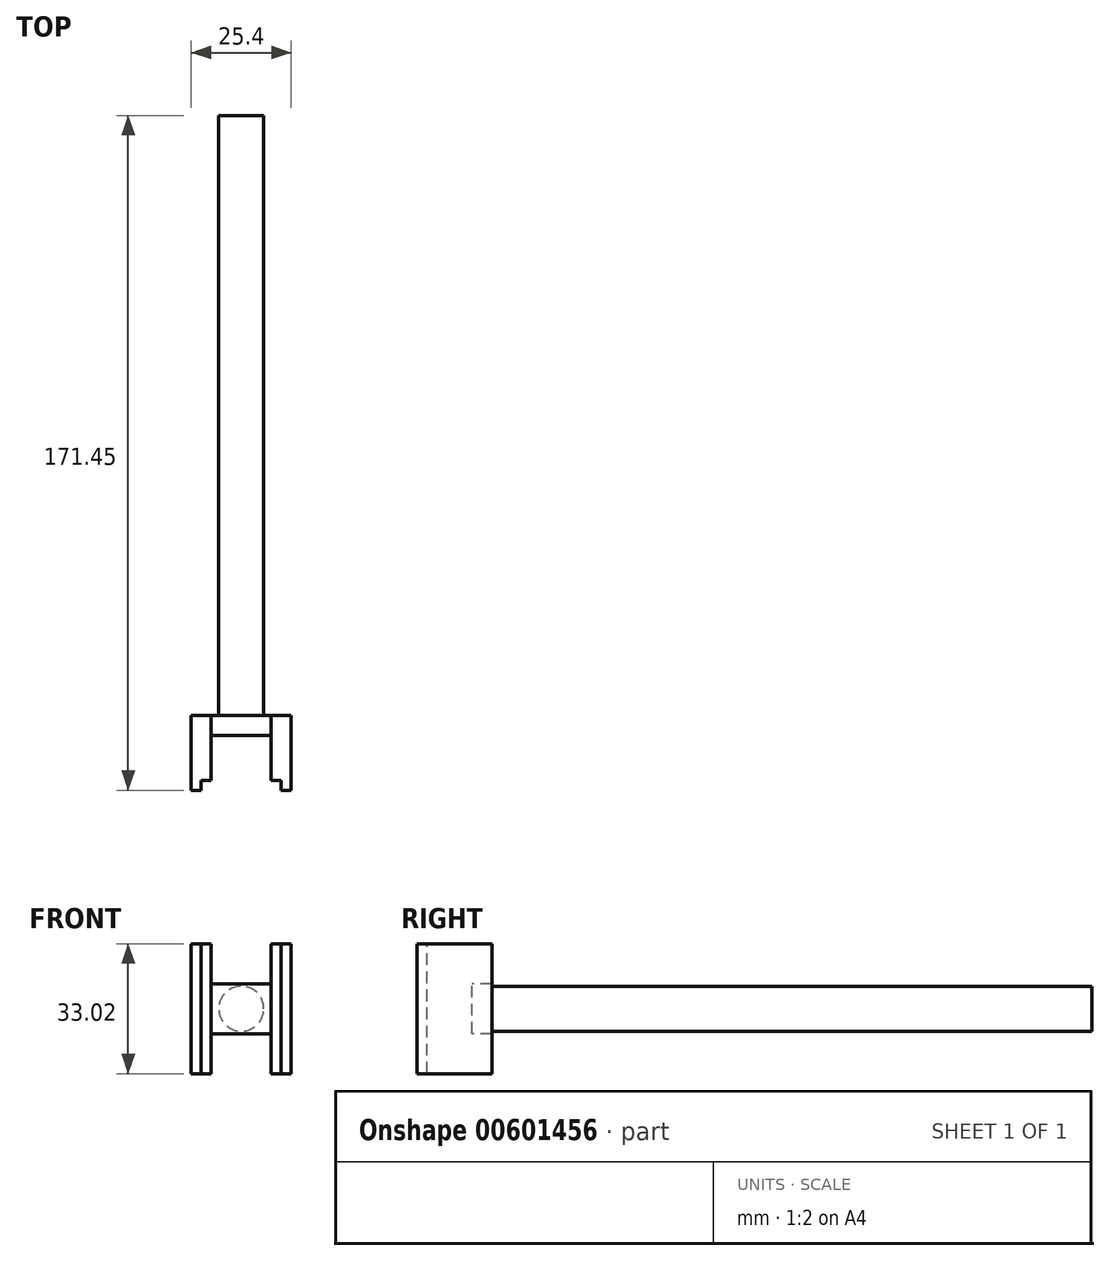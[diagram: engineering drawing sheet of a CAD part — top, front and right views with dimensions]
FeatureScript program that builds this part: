
annotation { "Feature Type Name" : "Feature", "Feature Type Description" : "" }
export const myFeature = defineFeature(function(context is Context, id is Id, definition is map)
    precondition{}
    {
        {
            var Q0;
            Q0=qCreatedBy(makeId("Front.planeOp"),FACE);
            var sketch = newSketch(context, id + "F0", { "sketchPlane" : qUnion([Q0])});
            skLineSegment(sketch, "E0.bottom", {"start": v(0, 0) * mm, "end": v(25.4, 0) * mm});
            skLineSegment(sketch, "E0.top", {"start": v(0, 33.02) * mm, "end": v(25.4, 33.02) * mm});
            skLineSegment(sketch, "E0.left", {"start": v(0, 0) * mm, "end": v(0, 33.02) * mm});
            skLineSegment(sketch, "E0.right", {"start": v(25.4, 0) * mm, "end": v(25.4, 33.02) * mm});
            skSolve(sketch);
        }
        {
            var Q0;
            Q0=makeQuery(id+"F0.imprint","IMPRINT",FACE,{"disambiguationData":[TD([[makeQuery(id+"F0.imprint","IMPRINT",EDGE,{"derivedFrom":sQuery(id+"F0.wireOp",EDGE,"E0.bottom")}),1.0]])]});
            var sketch = newSketch(context, id + "F1", { "sketchPlane" : qUnion([Q0])});
            skSolve(sketch);
        }
        {
            var Q0;
            Q0=makeQuery(id+"F0.imprint","IMPRINT",FACE,{"disambiguationData":[TD([[makeQuery(id+"F0.imprint","IMPRINT",EDGE,{"derivedFrom":sQuery(id+"F0.wireOp",EDGE,"E0.bottom")}),1.0]])]});
            extrude(context, id + "F2", {"entities" : qUnion([Q0]), "oppositeDirection" : true, "depth" : 19.05 * mm, "offsetDistance" : 25.4 * mm});
        }
        {
            var Q0;
            Q0=makeQuery(id+"F2.opExtrude","SWEPT_FACE",FACE,{"disambiguationData":[OSD([sQuery(id+"F0.wireOp",EDGE,"E0.top")])]});
            var sketch = newSketch(context, id + "F3", { "sketchPlane" : qUnion([Q0])});
            skLineSegment(sketch, "E1.bottom", {"start": v(5.08, 0) * mm, "end": v(20.32, 0) * mm});
            skLineSegment(sketch, "E1.top", {"start": v(5.08, 13.97) * mm, "end": v(20.32, 13.97) * mm});
            skLineSegment(sketch, "E1.left", {"start": v(5.08, 0) * mm, "end": v(5.08, 13.97) * mm});
            skLineSegment(sketch, "E1.right", {"start": v(20.32, 0) * mm, "end": v(20.32, 13.97) * mm});
            skSolve(sketch);
        }
        {
            var Q0;
            Q0=makeQuery(id+"F3.imprint","IMPRINT",FACE,{"disambiguationData":[TD([[makeQuery(id+"F3.imprint","IMPRINT",EDGE,{"derivedFrom":sQuery(id+"F3.wireOp",EDGE,"E1.bottom")}),1.0]])]});
            extrude(context, id + "F4", {"entities" : qUnion([Q0]), "operationType" : NewBodyOperationType.REMOVE, "endBound" : BoundingType.THROUGH_ALL, "oppositeDirection" : true, "depth" : 25.4 * mm, "offsetDistance" : 25.4 * mm});
        }
        {
            var Q0;
            Q0=makeQuery(id+"F2.opExtrude","SWEPT_FACE",FACE,{"disambiguationData":[OSD([sQuery(id+"F0.wireOp",EDGE,"E0.top")])]});
            var sketch = newSketch(context, id + "F5", { "sketchPlane" : qUnion([Q0])});
            skLineSegment(sketch, "E2.bottom", {"start": v(2.54, 0) * mm, "end": v(5.08, 0) * mm});
            skLineSegment(sketch, "E2.top", {"start": v(2.54, 2.54) * mm, "end": v(5.08, 2.54) * mm});
            skLineSegment(sketch, "E2.left", {"start": v(2.54, 0) * mm, "end": v(2.54, 2.54) * mm});
            skLineSegment(sketch, "E2.right", {"start": v(5.08, 0) * mm, "end": v(5.08, 2.54) * mm});
            skLineSegment(sketch, "E3.bottom", {"start": v(20.32, 0) * mm, "end": v(22.86, 0) * mm});
            skLineSegment(sketch, "E3.top", {"start": v(20.32, 2.54) * mm, "end": v(22.86, 2.54) * mm});
            skLineSegment(sketch, "E3.left", {"start": v(20.32, 0) * mm, "end": v(20.32, 2.54) * mm});
            skLineSegment(sketch, "E3.right", {"start": v(22.86, 0) * mm, "end": v(22.86, 2.54) * mm});
            skSolve(sketch);
        }
        {
            var Q0;
            Q0=makeQuery(id+"F5.imprint","IMPRINT",FACE,{"disambiguationData":[TD([[makeQuery(id+"F5.imprint","IMPRINT",EDGE,{"derivedFrom":sQuery(id+"F5.wireOp",EDGE,"E2.bottom")}),1.0]])]});
            var Q1;
            Q1=makeQuery(id+"F5.imprint","IMPRINT",FACE,{"disambiguationData":[TD([[makeQuery(id+"F5.imprint","IMPRINT",EDGE,{"derivedFrom":sQuery(id+"F5.wireOp",EDGE,"E3.bottom")}),1.0]])]});
            extrude(context, id + "F6", {"entities" : qUnion([Q0, Q1]), "operationType" : NewBodyOperationType.REMOVE, "endBound" : BoundingType.THROUGH_ALL, "oppositeDirection" : true, "depth" : 25.4 * mm, "offsetDistance" : 25.4 * mm});
        }
        {
            var Q0;
            Q0=makeQuery(id+"F1.imprint","IMPRINT",FACE,{"disambiguationData":[TD([[makeQuery(id+"F1.imprint","IMPRINT",EDGE,{"derivedFrom":makeQuery(id+"F0.imprint","IMPRINT",EDGE,{"derivedFrom":sQuery(id+"F0.wireOp",EDGE,"E0.bottom")})}),1.0]])]});
            var sketch = newSketch(context, id + "F7", { "sketchPlane" : qUnion([Q0])});
            skSolve(sketch);
        }
        {
            var Q0;
            Q0=makeQuery(id+"F7.imprint","IMPRINT",FACE,{"disambiguationData":[TD([[makeQuery(id+"F7.imprint","IMPRINT",EDGE,{"derivedFrom":makeQuery(id+"F1.imprint","IMPRINT",EDGE,{"derivedFrom":makeQuery(id+"F0.imprint","IMPRINT",EDGE,{"derivedFrom":sQuery(id+"F0.wireOp",EDGE,"E0.bottom")})})}),1.0]])]});
            var sketch = newSketch(context, id + "F8", { "sketchPlane" : qUnion([Q0])});
            skLineSegment(sketch, "E4.bottom", {"start": v(5.08, 33.06) * mm, "end": v(20.32, 33.06) * mm});
            skLineSegment(sketch, "E4.top", {"start": v(5.08, 22.86) * mm, "end": v(20.32, 22.86) * mm});
            skLineSegment(sketch, "E4.left", {"start": v(5.08, 33.06) * mm, "end": v(5.08, 22.86) * mm});
            skLineSegment(sketch, "E4.right", {"start": v(20.32, 33.06) * mm, "end": v(20.32, 22.86) * mm});
            skLineSegment(sketch, "E5.bottom", {"start": v(5.08, 0) * mm, "end": v(20.32, 0) * mm});
            skLineSegment(sketch, "E5.top", {"start": v(5.08, 10.16) * mm, "end": v(20.32, 10.16) * mm});
            skLineSegment(sketch, "E5.left", {"start": v(5.08, 0) * mm, "end": v(5.08, 10.16) * mm});
            skLineSegment(sketch, "E5.right", {"start": v(20.32, 0) * mm, "end": v(20.32, 10.16) * mm});
            skSolve(sketch);
        }
        {
            var Q0;
            Q0 = qSketchRegion(id + "F8", true);
            extrude(context, id + "F9", {"entities" : qUnion([Q0]), "operationType" : NewBodyOperationType.REMOVE, "endBound" : BoundingType.THROUGH_ALL, "oppositeDirection" : true, "depth" : 25.4 * mm, "offsetDistance" : 25.4 * mm});
        }
        {
            var Q0;
            Q0=makeQuery(id+"F2.opExtrude","CAP_FACE",FACE,{"disambiguationData":[OSD([sQuery(id+"F0.wireOp",EDGE,"E0.bottom"),sQuery(id+"F0.wireOp",EDGE,"E0.top"),sQuery(id+"F0.wireOp",EDGE,"E0.left"),sQuery(id+"F0.wireOp",EDGE,"E0.right")])],"isStart":false});
            var sketch = newSketch(context, id + "F10", { "sketchPlane" : qUnion([Q0])});
            skSolve(sketch);
        }
        {
            var Q0;
            {var subQ1=sQuery(id+"F0.wireOp",EDGE,"E0.left");Q0=makeQuery(id+"F10.imprint","IMPRINT",FACE,{"disambiguationData":[TD([[makeQuery(id+"F10.imprint","IMPRINT",EDGE,{"derivedFrom":makeQuery(id+"F2.opExtrude","CAP_EDGE",EDGE,{"disambiguationData":[OSD([subQ1])],"isStart":false})}),1.0]])]});}
            var sketch = newSketch(context, id + "F11", { "sketchPlane" : qUnion([Q0])});
            skCircle(sketch, "E6", {"center": v(-12.7, 16.51) * mm, "radius": 5.72 * mm});
            skSolve(sketch);
        }
        {
            var Q0;
            Q0=makeQuery(id+"F11.imprint","IMPRINT",FACE,{"disambiguationData":[TD([[makeQuery(id+"F11.imprint","IMPRINT",EDGE,{"derivedFrom":sQuery(id+"F11.wireOp",EDGE,"E6")}),1.0]])]});
            extrude(context, id + "F12", {"entities" : qUnion([Q0]), "operationType" : NewBodyOperationType.ADD, "depth" : 152.4 * mm, "offsetDistance" : 25.4 * mm});
        }
    });
